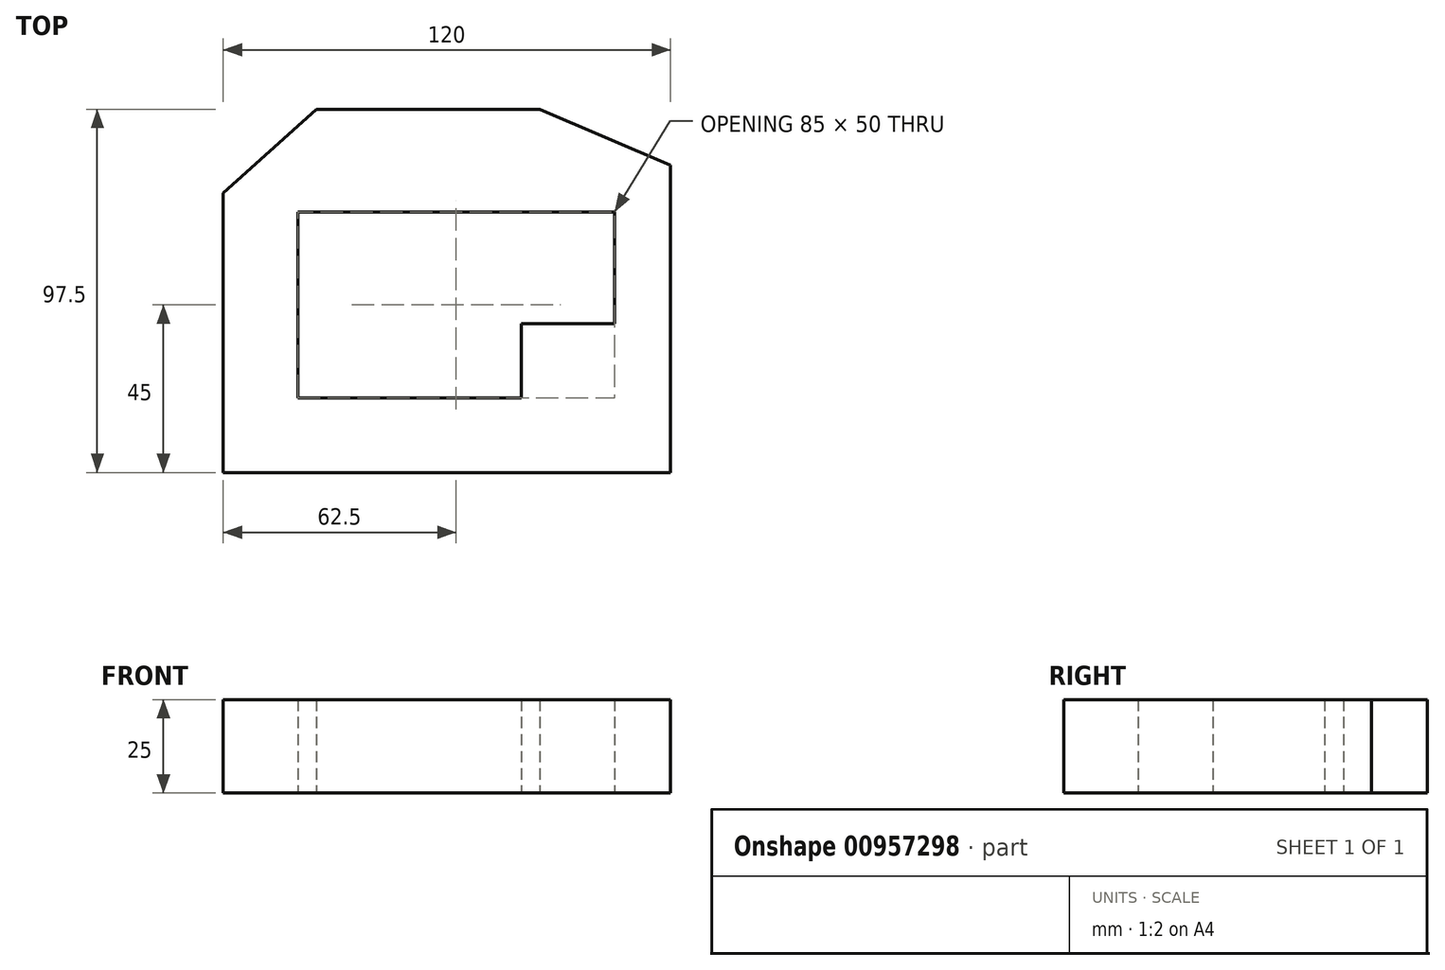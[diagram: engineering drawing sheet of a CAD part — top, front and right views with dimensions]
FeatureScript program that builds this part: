
annotation { "Feature Type Name" : "Feature", "Feature Type Description" : "" }
export const myFeature = defineFeature(function(context is Context, id is Id, definition is map)
    precondition{}
    {
        {
            var Q0;
            Q0=qCreatedBy(makeId("Top.planeOp"),FACE);
            var sketch = newSketch(context, id + "F0", { "sketchPlane" : qUnion([Q0])});
            skLineSegment(sketch, "E0", {"start": v(0, 0) * mm, "end": v(0, 82.5) * mm});
            skLineSegment(sketch, "E1", {"start": v(0, 82.5) * mm, "end": v(-35, 97.5) * mm});
            skLineSegment(sketch, "E2", {"start": v(-35, 97.5) * mm, "end": v(-95, 97.5) * mm});
            skLineSegment(sketch, "E3", {"start": v(-95, 97.5) * mm, "end": v(-120, 75) * mm});
            skLineSegment(sketch, "E4", {"start": v(-120, 75) * mm, "end": v(-120, 0) * mm});
            skLineSegment(sketch, "E5", {"start": v(-120, 0) * mm, "end": v(0, 0) * mm});
            skLineSegment(sketch, "E6", {"start": v(-100, 70) * mm, "end": v(-100, 20) * mm});
            skLineSegment(sketch, "E7", {"start": v(-100, 20) * mm, "end": v(-40, 20) * mm});
            skLineSegment(sketch, "E8", {"start": v(-40, 20) * mm, "end": v(-40, 40) * mm});
            skLineSegment(sketch, "E9", {"start": v(-40, 40) * mm, "end": v(-15, 40) * mm});
            skLineSegment(sketch, "E10", {"start": v(-15, 70) * mm, "end": v(-15, 40) * mm});
            skLineSegment(sketch, "E11", {"start": v(-15, 70) * mm, "end": v(-100, 70) * mm});
            skSolve(sketch);
        }
        {
            var Q0;
            Q0=makeQuery(id+"F0.imprint","IMPRINT",FACE,{"disambiguationData":[TD([[makeQuery(id+"F0.imprint","IMPRINT",EDGE,{"derivedFrom":sQuery(id+"F0.wireOp",EDGE,"E0")}),1.0]])]});
            extrude(context, id + "F1", {"entities" : qUnion([Q0]), "depth" : 25 * mm, "offsetDistance" : 25 * mm});
        }
    });
